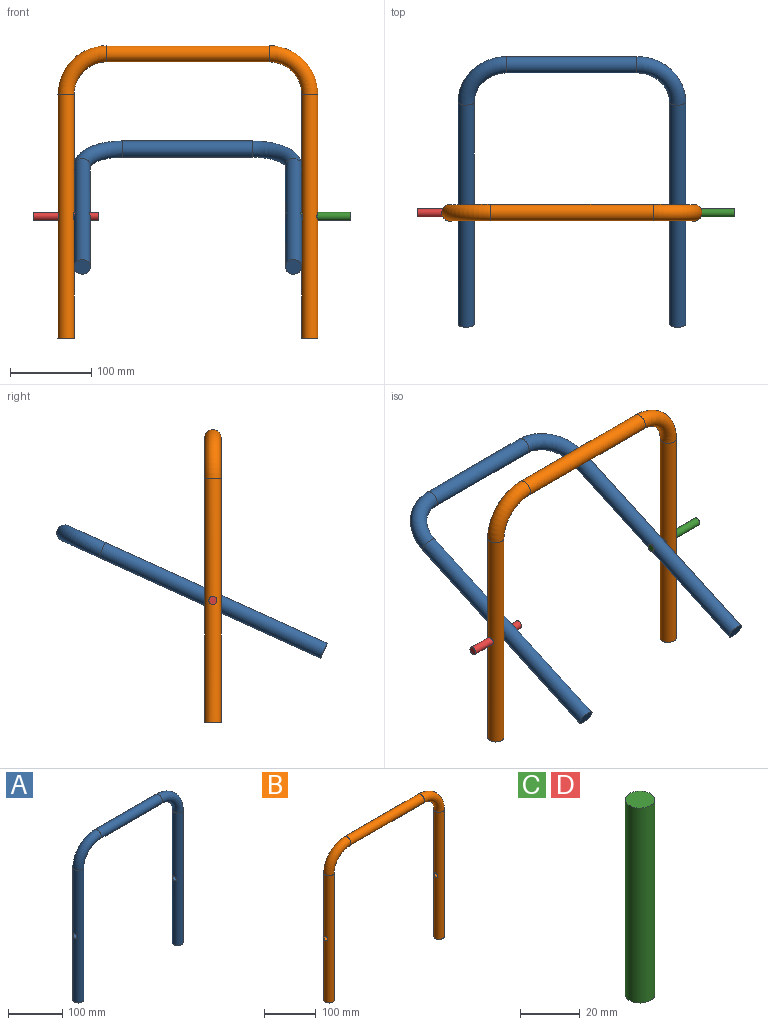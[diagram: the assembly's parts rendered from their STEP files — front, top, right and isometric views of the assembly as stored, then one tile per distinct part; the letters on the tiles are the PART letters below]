
ASSEMBLY  parts=4 mates=3
PART A: 9 faces, bbox 289.9x20x364.9 mm
  f0: plane 20x20mm, normal (0,0,-1), area 314.2mm2, adj f2
  f1: plane 20x20mm, normal (0,0,-1), area 314.2mm2, adj f6
  f2: cylinder r=10mm len=300mm, axis (0,0,1), area 18687mm2, adj f0,f3,f8
  f3: torus R=50mm, axis (0,1,0), area 4934.8mm2, adj f2,f4
  f4: cylinder r=10mm len=160mm, axis (1,0,0), area 10053.1mm2, adj f3,f5
  f5: torus R=50mm, axis (0,1,0), area 4934.8mm2, adj f4,f6
  f6: cylinder r=10mm len=300mm, axis (0,0,-1), area 18687.1mm2, adj f1,f5,f7
  f7: cylinder r=5mm len=20mm, axis (1,0,0), area 587mm2, adj f6
  f8: cylinder r=5mm len=20mm, axis (1,0,0), area 587mm2, adj f2
PART B: 9 faces, bbox 329.9x20x364.9 mm
  f0: plane 20x20mm, normal (0,0,-1), area 314.2mm2, adj f2
  f1: plane 20x20mm, normal (0,0,-1), area 314.2mm2, adj f6
  f2: cylinder r=10mm len=300mm, axis (0,0,1), area 18687mm2, adj f0,f3,f8
  f3: torus R=50mm, axis (0,1,0), area 4934.8mm2, adj f2,f4
  f4: cylinder r=10mm len=200mm, axis (1,0,0), area 12566.4mm2, adj f3,f5
  f5: torus R=50mm, axis (0,1,0), area 4934.8mm2, adj f4,f6
  f6: cylinder r=10mm len=300mm, axis (0,0,-1), area 18687.1mm2, adj f1,f5,f7
  f7: cylinder r=5mm len=20mm, axis (1,0,0), area 587mm2, adj f6
  f8: cylinder r=5mm len=20mm, axis (1,0,0), area 587mm2, adj f2
PART C: 3 faces, bbox 9.9x9.9x80 mm
  f0: cylinder r=4.95mm len=80mm, axis (0,0,-1), area 2488.1mm2, adj f1,f2
  f1: plane 9.9x9.9mm, normal (0,0,1), area 77mm2, adj f0
  f2: plane 9.9x9.9mm, normal (0,0,-1), area 77mm2, adj f0
PART D: same geometry as C
PLACE A rot(axis=(-1,0,0),65.6deg) t=(-180.41,-28.34,-6.47)mm
PLACE B t=(-200.41,108.22,-94.39)mm fixed
PLACE C rot(axis=(0,1,0),90deg) t=(69.59,114.35,59.91)mm
PLACE D rot(axis=(0.67,0.31,0.67),145.5deg) t=(-240.41,100.97,57.48)mm
MATE cylindrical D.f0 <-> A.f7  axis (1,0,0) through (-160.41,108.22,55.61)mm
MATE cylindrical C.f0 <-> B.f7  axis (1,0,0) through (149.59,108.22,55.61)mm
MATE cylindrical B.f7 <-> D.f0  axis (1,0,0) through (-200.41,108.22,55.61)mm
